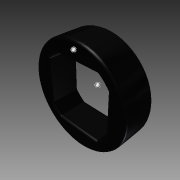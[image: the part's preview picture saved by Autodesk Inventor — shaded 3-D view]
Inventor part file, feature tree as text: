
AUTODESK INVENTOR PART (.ipt)
format: ipt  version: 2015 (Build 190159000, 159)  size: 225,792 bytes
history: native  units: in
note: dims shown in document units (in); Inventor stores cm internally (conversion verified against a paired STEP export)
features: fillet x1, other x1, imported_body x1
ambient origin geometry x8: Origin, YZ Plane, XZ Plane, XY Plane, X Axis, Y Axis, Z Axis, Center Point
bodies: Body1 (feature_tree)
feature tree (3):
  fillet  "Fillet1"  [1 undecoded]
  other  "Spacer HS 0.25 unit"
  imported_body  "Base1"
note: 1 required parameter value undecoded (feature->parameter linkage not recoverable at this tier; creation-order binding heuristic only, values carry confidence <= 0.55)
